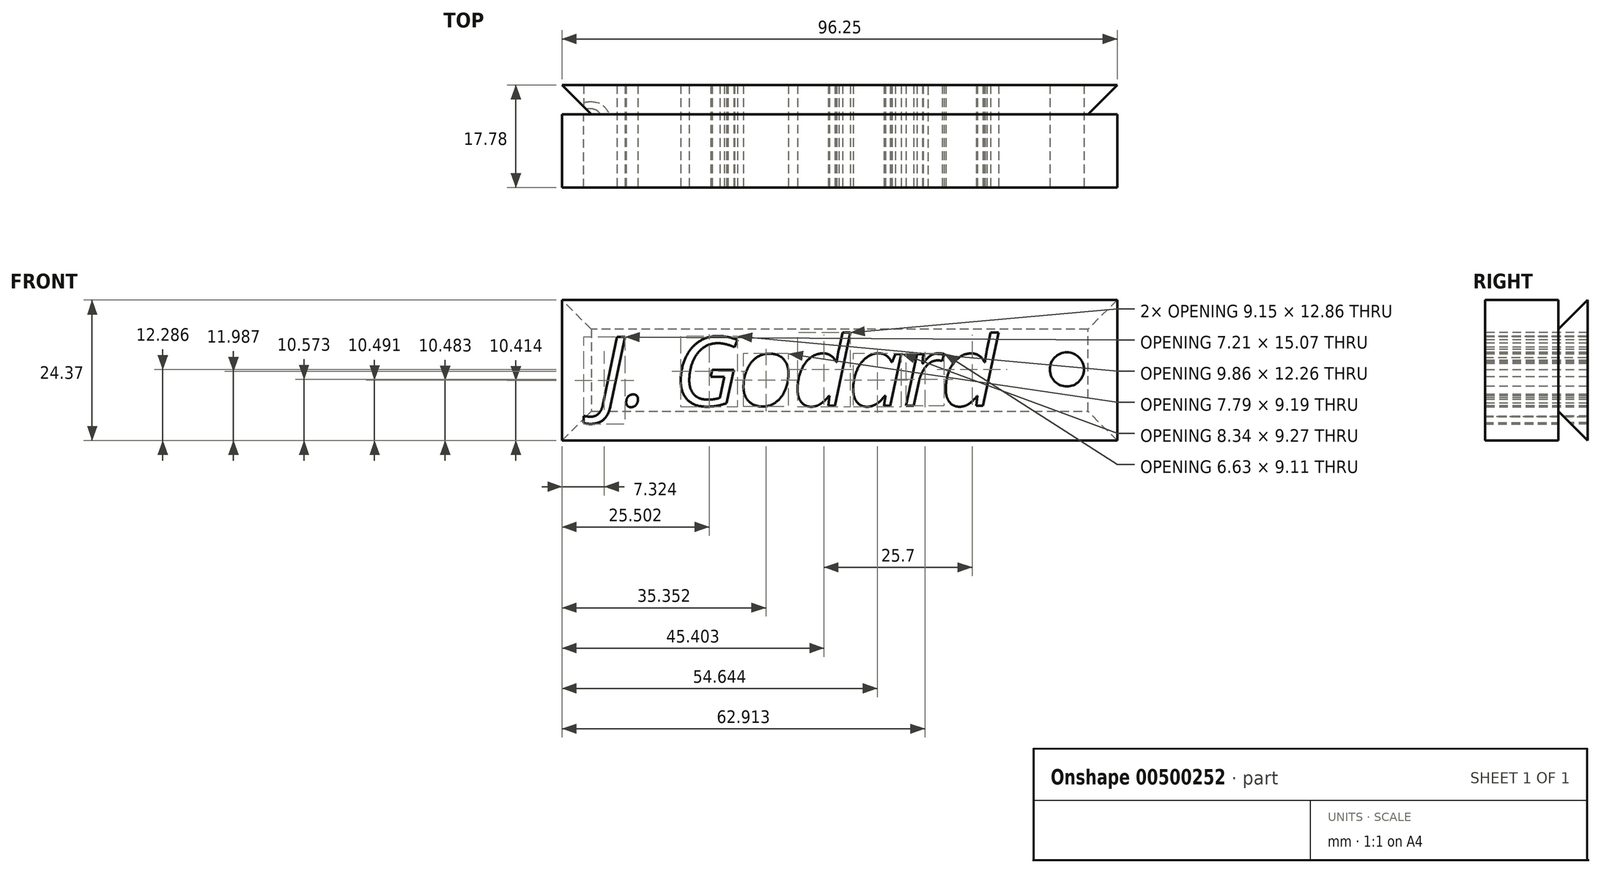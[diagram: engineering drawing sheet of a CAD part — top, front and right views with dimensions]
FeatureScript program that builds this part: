
annotation { "Feature Type Name" : "Feature", "Feature Type Description" : "" }
export const myFeature = defineFeature(function(context is Context, id is Id, definition is map)
    precondition{}
    {
        {
            var Q0;
            Q0=qCreatedBy(makeId("Front.planeOp"),FACE);
            var sketch = newSketch(context, id + "F0", { "sketchPlane" : qUnion([Q0])});
            skLineSegment(sketch, "E0.bottom", {"start": v(-69.18, 41.2) * mm, "end": v(27.07, 41.2) * mm});
            skLineSegment(sketch, "E0.top", {"start": v(-69.18, 16.84) * mm, "end": v(27.07, 16.84) * mm});
            skLineSegment(sketch, "E0.left", {"start": v(-69.18, 41.2) * mm, "end": v(-69.18, 16.84) * mm});
            skLineSegment(sketch, "E0.right", {"start": v(27.07, 41.2) * mm, "end": v(27.07, 16.84) * mm});
            skText(sketch, "E1", { "text": "J. Godard", "fontName": "OpenSans-Italic.ttf"});
            skCircle(sketch, "E2", {"center": v(18.35, 29.18) * mm, "radius": 2.96 * mm});
            const initialGuessF0  = {"E1": [-0.06286, 0.02286, 1, 0, 0.01203]};
            skSetInitialGuess(sketch, initialGuessF0);
            skSolve(sketch);
        }
        {
            var Q0;
            Q0 = qSketchRegion(id + "F0", true);
            extrude(context, id + "F1", {"entities" : qUnion([Q0]), "oppositeDirection" : true, "depth" : 5.08 * mm});
        }
        {
            var Q0;
            Q0=makeQuery(id+"F1.opExtrude","CAP_EDGE",EDGE,{"disambiguationData":[OSD([sQuery(id+"F0.wireOp",EDGE,"E0.right")])],"isStart":true});
            var Q1;
            Q1=makeQuery(id+"F1.opExtrude","CAP_EDGE",EDGE,{"disambiguationData":[OSD([sQuery(id+"F0.wireOp",EDGE,"E0.top")])],"isStart":true});
            var Q2;
            Q2=makeQuery(id+"F1.opExtrude","CAP_EDGE",EDGE,{"disambiguationData":[OSD([sQuery(id+"F0.wireOp",EDGE,"E0.left")])],"isStart":true});
            var Q3;
            Q3=makeQuery(id+"F1.opExtrude","CAP_EDGE",EDGE,{"disambiguationData":[OSD([sQuery(id+"F0.wireOp",EDGE,"E0.bottom")])],"isStart":true});
            chamfer(context, id + "F2", {"entities" : qUnion([Q0, Q1, Q2, Q3]), "width" : 5.08 * mm, "tangentPropagation" : true});
        }
        {
            var Q0;
            Q0 = qSketchRegion(id + "F0", true);
            extrude(context, id + "F3", {"entities" : qUnion([Q0]), "operationType" : NewBodyOperationType.ADD, "depth" : 12.7 * mm});
        }
    });
